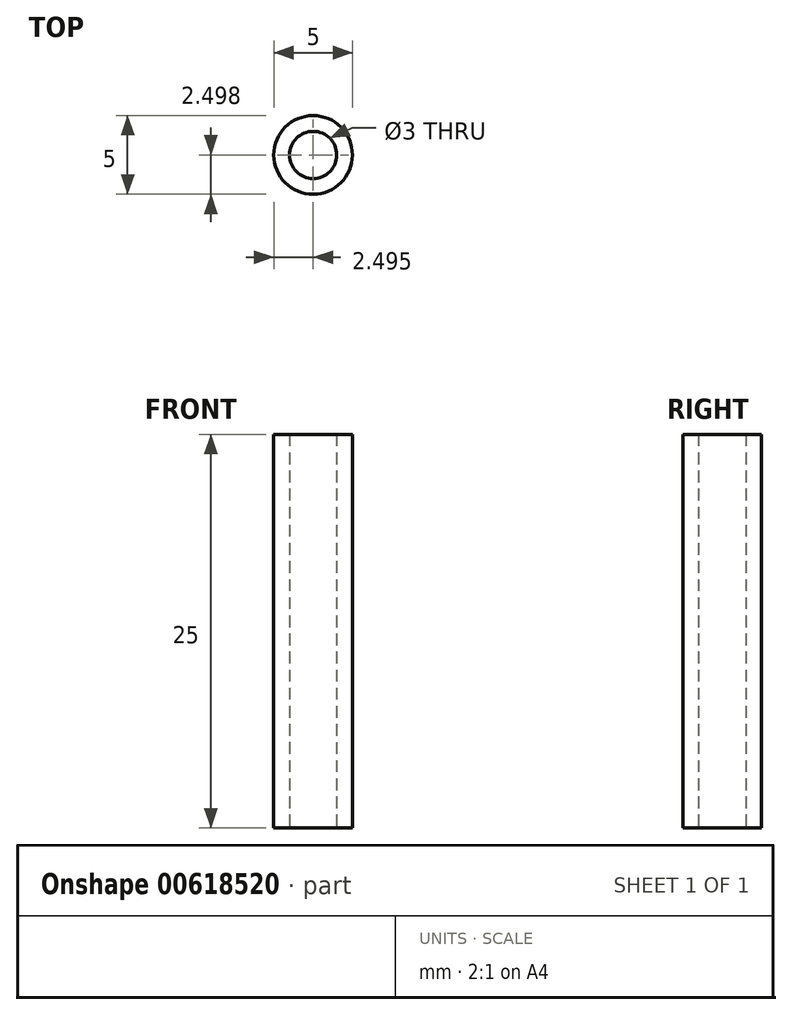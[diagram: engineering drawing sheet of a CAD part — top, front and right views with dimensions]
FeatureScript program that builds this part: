
annotation { "Feature Type Name" : "Feature", "Feature Type Description" : "" }
export const myFeature = defineFeature(function(context is Context, id is Id, definition is map)
    precondition{}
    {
        {
            var Q0;
            Q0=qCreatedBy(makeId("Top.planeOp"),FACE);
            var sketch = newSketch(context, id + "F0", { "sketchPlane" : qUnion([Q0])});
            skCircle(sketch, "E0", {"center": v(-39.18, 31.74) * mm, "radius": 2.5 * mm});
            skCircle(sketch, "E1", {"center": v(-39.18, 31.74) * mm, "radius": 1.5 * mm});
            skSolve(sketch);
        }
        {
            var Q0;
            Q0 = qSketchRegion(id + "F0", true);
            extrude(context, id + "F1", {"entities" : qUnion([Q0]), "depth" : 25 * mm, "offsetDistance" : 25 * mm});
        }
    });
